# Revit family: BOS-Schattennutzarge-15NbEud-MW_Familie
name_source: partatom
category: Türen
revit_build: Autodesk Revit 2017 (Build: 20160225_1515(x64)
units: mm (PartAtom-declared; Revit-internal decimal feet)

## family parameters
Basisbauteil = Wand
Beim Laden mit Abzugskörper schneiden = Nein
Gemeinsam genutzt = Nein
Immer vertikal = Ja
Raumberechnungspunkt = Ja

## types (4) — shared parameters
BBL1 Bandbezugslinie   Hinge Position 1 = 241 mm  [stored 0.790682 ft]
BE max. = 100 mm  [stored 0.328084 ft]
Bauelement = BOS Stahlzarge
Blechstärke = 1.5 mm  [stored 0.00492126 ft]
Dichtung 1 = Ja
Drehpunkt Warnung sichtbar = Ja
Drehpunktreferenz horizontal = 500 mm  [stored 1.64042 ft]
FMB max. = 1342 mm  [stored 4.40289 ft]
FMB min. = 591 mm  [stored 1.93898 ft]
FMH max. = 2858 mm  [stored 9.37664 ft]
FMH min. = 1608 mm  [stored 5.27559 ft]
Falzaufschlag = 15 mm  [stored 0.0492126 ft]
Falztiefe 2 = 25 mm  [stored 0.082021 ft]
Funktion = Innen
Hersteller = BOS GmbH Best Of Steel, Lütkenfelde 4, D-48282 Emsdetten
Info-Texte sichtbar = Ja
Information in English = Nein
Leibungstiefe max. = 40 mm  [stored 0.131234 ft]
Leibungstiefe min. = 40 mm  [stored 0.131234 ft]
Material = grundiert, feuerverzinktes Feinblech nach DIN EN 10143
Material - Bänder = <Nach Kategorie>
Material - Dichtung = <Nach Kategorie>
Material - Drückergarnitur = <Nach Kategorie>
Material - Türblatt = <Nach Kategorie>
Material - Zarge = <Nach Kategorie>
Putzwinkel max. = 28 mm  [stored 0.0918635 ft]
Putzwinkel min. = 10 mm  [stored 0.0328084 ft]
Schattennutbreite max. = 15 mm  [stored 0.0492126 ft]
Schattennutbreite min. = 15 mm  [stored 0.0492126 ft]
Schattennuttiefe max. = 11.5 mm  [stored 0.0377297 ft]
Schattennuttiefe min. = 11.5 mm  [stored 0.0377297 ft]
Sickentiefe = 10 mm  [stored 0.0328084 ft]
Spiegel vorne min. = 30 mm  [stored 0.0984252 ft]
Technische Infos rund um die Stahlzarge = www.BestOfSteel.de/tools-downloads/technische-infos-rund-um-die-stahlzarge/
Typenbild = <Keine Auswahl>
Türblattabstand 2 = 4.5 mm  [stored 0.0147638 ft]
Türblattabstand 3 = 4.5 mm  [stored 0.0147638 ft]
Türblattabstand links-rechts = 3.5 mm  [stored 0.0114829 ft]
Türblattaufschlag = 13 mm
URL = www.BestOfSteel.de/stahlzargen/zargen-fuer-drehfluegeltueren/schattennutzargen/eckzargen/
Öffnungswinkel max. = 180.00°
Öffnungswinkel min. = 0.00°
zero-valued in all types: Breite, Dicke, Rohbaubreite, Rohbauhöhe

## per-type parameters (varying)
| type | 15NbEsFd | 15NbEsd | 15NbEuFd | 15NbEud | Beschreibung | Dichtung 2 | Doppelfalz | Drehpunktabstand (FM) horizontal | Drehpunktabstand (SP) vertikal | Einfachfalz | Falzaufschlag gesamt | Falztiefe | Falztiefe gesamt | Gefälzt | Stumpf | Türblattabstand 1 | Türblattstärke | Türblattstärke 1 | Türblattstärke 2 | Türblattstärke 3 | Türblattversatz  horizontal | Türblattversatz vertikal |
| 15NbEud | Nein | Nein | Nein | Ja | Schattennutzarge als Eckprofil für Mauerwerk, gefälzt | Nein | Nein | 21 mm  [stored 0.0688976 ft] | 12.5 mm  [stored 0.0410105 ft] | Ja | 15 mm  [stored 0.0492126 ft] | 28.5 mm  [stored 0.0935039 ft] | 28.5 mm  [stored 0.0935039 ft] | Ja | Nein | 1.5 mm  [stored 0.00492126 ft] | 40 mm  [stored 0.131234 ft] | 14.5 mm  [stored 0.0475722 ft] | 25.5 mm  [stored 0.0836614 ft] | 0 mm  [stored 0 ft] | 11.5 mm  [stored 0.0377297 ft] | -3.5 mm  [stored -0.0114829 ft] |
| 15NbEuFd | Nein | Nein | Ja | Nein | Schattennutzarge als Eckprofil für Mauerwerk, gefälzt, mit Doppelfalz | Ja | Ja | 21 mm  [stored 0.0688976 ft] | 12.5 mm  [stored 0.0410105 ft] | Nein | 30 mm  [stored 0.0984252 ft] | 28.5 mm  [stored 0.0935039 ft] | 53.5 mm  [stored 0.175525 ft] | Ja | Nein | 1.5 mm  [stored 0.00492126 ft] | 65 mm  [stored 0.213255 ft] | 14.5 mm  [stored 0.0475722 ft] | 25.5 mm  [stored 0.0836614 ft] | 25 mm  [stored 0.082021 ft] | 11.5 mm  [stored 0.0377297 ft] | -3.5 mm  [stored -0.0114829 ft] |
| 15NbEsd | Nein | Ja | Nein | Nein | Schattennutzarge als Eckprofil für Mauerwerk, stumpf | Nein | Nein | 2.5 mm  [stored 0.0082021 ft] | 13.5 mm  [stored 0.0442913 ft] | Ja | 15 mm  [stored 0.0492126 ft] | 46.5 mm  [stored 0.152559 ft] | 46.5 mm  [stored 0.152559 ft] | Nein | Ja | -2 mm  [stored -0.00656168 ft] | 40 mm  [stored 0.131234 ft] | 0 mm  [stored 0 ft] | 40 mm  [stored 0.131234 ft] | 0 mm  [stored 0 ft] | 6 mm  [stored 0.019685 ft] | 15.5 mm  [stored 0.050853 ft] |
| 15NbEsFd | Ja | Nein | Nein | Nein | Schattennutzarge als Eckprofil für Mauerwerk, stumpf, mit Doppelfalz | Ja | Ja | 2.5 mm  [stored 0.0082021 ft] | 13.5 mm  [stored 0.0442913 ft] | Nein | 30 mm  [stored 0.0984252 ft] | 46.5 mm  [stored 0.152559 ft] | 71.5 mm | Nein | Ja | -2 mm  [stored -0.00656168 ft] | 65 mm  [stored 0.213255 ft] | 0 mm  [stored 0 ft] | 40 mm  [stored 0.131234 ft] | 25 mm  [stored 0.082021 ft] | 6 mm  [stored 0.019685 ft] | 15.5 mm  [stored 0.050853 ft] |

note: column(s) folded — value = type name in every type: Modell

note: [stored X ft] marks values corroborated as IEEE doubles in the binary element streams (Revit-internal decimal feet)
